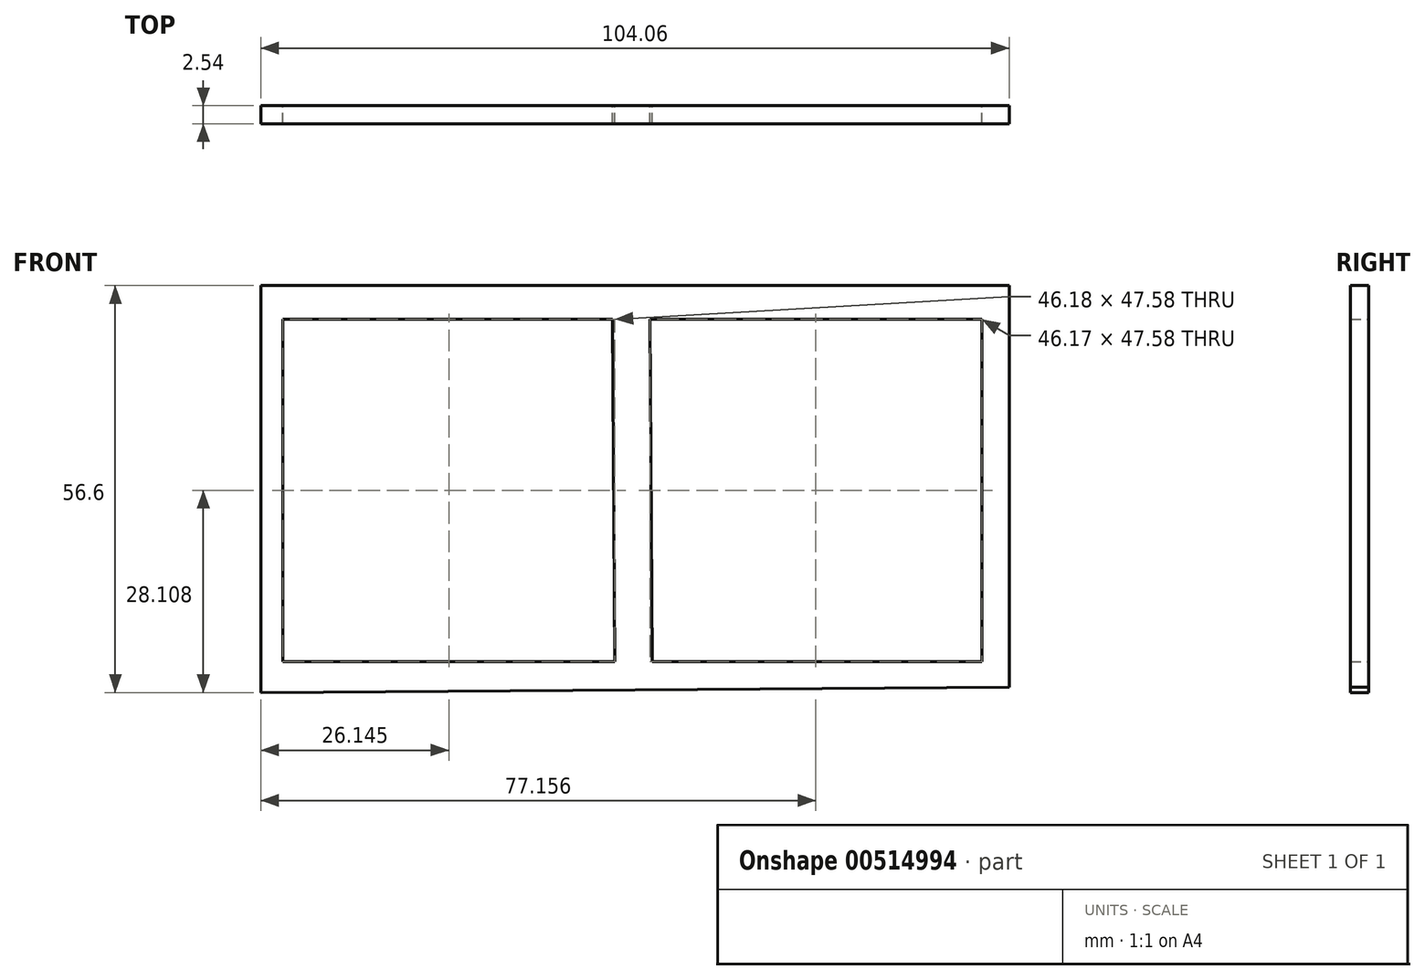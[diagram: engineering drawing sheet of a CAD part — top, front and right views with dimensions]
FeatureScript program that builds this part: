
annotation { "Feature Type Name" : "Feature", "Feature Type Description" : "" }
export const myFeature = defineFeature(function(context is Context, id is Id, definition is map)
    precondition{}
    {
        {
            var Q0;
            Q0=qCreatedBy(makeId("Front.planeOp"),FACE);
            var sketch = newSketch(context, id + "F0", { "sketchPlane" : qUnion([Q0])});
            skLineSegment(sketch, "E0", {"start": v(-48.85, 0) * mm, "end": v(-48.85, -56.6) * mm});
            skLineSegment(sketch, "E1", {"start": v(55.2, 0) * mm, "end": v(55.2, -55.84) * mm});
            skLineSegment(sketch, "E2", {"start": v(-48.85, 0) * mm, "end": v(55.2, 0) * mm});
            skLineSegment(sketch, "E3", {"start": v(55.2, -55.84) * mm, "end": v(-48.85, -56.6) * mm});
            skLineSegment(sketch, "E4", {"start": v(-45.8, 0) * mm, "end": v(-45.8, -56.6) * mm});
            skLineSegment(sketch, "E5", {"start": v(51.39, 0) * mm, "end": v(51.39, -55.87) * mm});
            skLineSegment(sketch, "E6", {"start": v(51.39, -55.87) * mm, "end": v(5.6, -56.2) * mm});
            skLineSegment(sketch, "E7", {"start": v(5.6, -56.2) * mm, "end": v(5.19, 0) * mm});
            skLineSegment(sketch, "E8", {"start": v(5.19, 0) * mm, "end": v(0, 0) * mm});
            skLineSegment(sketch, "E9", {"start": v(0, 0) * mm, "end": v(0.41, -56.2) * mm});
            skLineSegment(sketch, "E10", {"start": v(0.41, -56.2) * mm, "end": v(0.24, -32.44) * mm});
            skLineSegment(sketch, "E11", {"start": v(-45.8, -32.44) * mm, "end": v(-45.8, -28.3) * mm});
            skLineSegment(sketch, "E12", {"start": v(51.39, -28.3) * mm, "end": v(51.42, -32.44) * mm});
            skLineSegment(sketch, "E13", {"start": v(0.03, -4.7) * mm, "end": v(-45.8, -4.7) * mm});
            skLineSegment(sketch, "E14", {"start": v(-45.8, -4.7) * mm, "end": v(51.39, -4.7) * mm});
            skLineSegment(sketch, "E15", {"start": v(-45.8, -52.28) * mm, "end": v(51.39, -52.28) * mm});
            skSolve(sketch);
        }
        {
            var Q0;
            Q0 = qSketchRegion(id + "F0", true);
            var Q1;
            {var subQ0=sQuery(id+"F0.wireOp",EDGE,"ExMhsBPa-6qAW-O80y-Ojee-Cts7sl48W9Bo");Q1=makeQuery(id+"F0.imprint","IMPRINT",FACE,{"disambiguationData":[TD([[makeQuery(id+"F0.imprint","IMPRINT",EDGE,{"derivedFrom":subQ0}),-1.0]])]});}
            var Q2;
            {var subQ0=sQuery(id+"F0.wireOp",EDGE,"M9PzfAlS-UGA6-ydGa-gEp9-7Xn1z2u5VWK0");var subQ1=sQuery(id+"F0.wireOp",EDGE,"E7");var subQ2=makeQuery(id+"F0.imprint","INTERSECT",VERTEX,{"derivedFrom":[subQ1,subQ0]});Q2=makeQuery(id+"F0.imprint","IMPRINT",FACE,{"disambiguationData":[TD([[makeQuery(id+"F0.imprint","IMPRINT",EDGE,{"disambiguationData":[TD([[subQ2,-1.0]])],"derivedFrom":subQ1}),1.0]])]});}
            var Q3;
            {var subQ0=sQuery(id+"F0.wireOp",EDGE,"XySuXgOd-ghFN-Isic-zQOF-CCSOLOquDijq");var subQ1=sQuery(id+"F0.wireOp",EDGE,"E7");var subQ2=makeQuery(id+"F0.imprint","INTERSECT",VERTEX,{"derivedFrom":[subQ1,subQ0]});Q3=makeQuery(id+"F0.imprint","IMPRINT",FACE,{"disambiguationData":[TD([[makeQuery(id+"F0.imprint","IMPRINT",EDGE,{"disambiguationData":[TD([[subQ2,-1.0]])],"derivedFrom":subQ1}),1.0]])]});}
            var Q4;
            {var subQ0=sQuery(id+"F0.wireOp",EDGE,"E15");var subQ1=sQuery(id+"F0.wireOp",EDGE,"E7");var subQ2=makeQuery(id+"F0.imprint","INTERSECT",VERTEX,{"derivedFrom":[subQ1,subQ0]});Q4=makeQuery(id+"F0.imprint","IMPRINT",FACE,{"disambiguationData":[TD([[makeQuery(id+"F0.imprint","IMPRINT",EDGE,{"disambiguationData":[TD([[subQ2,-1.0]])],"derivedFrom":subQ1}),1.0]])]});}
            extrude(context, id + "F1", {"entities" : qUnion([Q0, Q1, Q2, Q3, Q4]), "depth" : 2.54 * mm, "offsetDistance" : 25.4 * mm});
        }
    });
